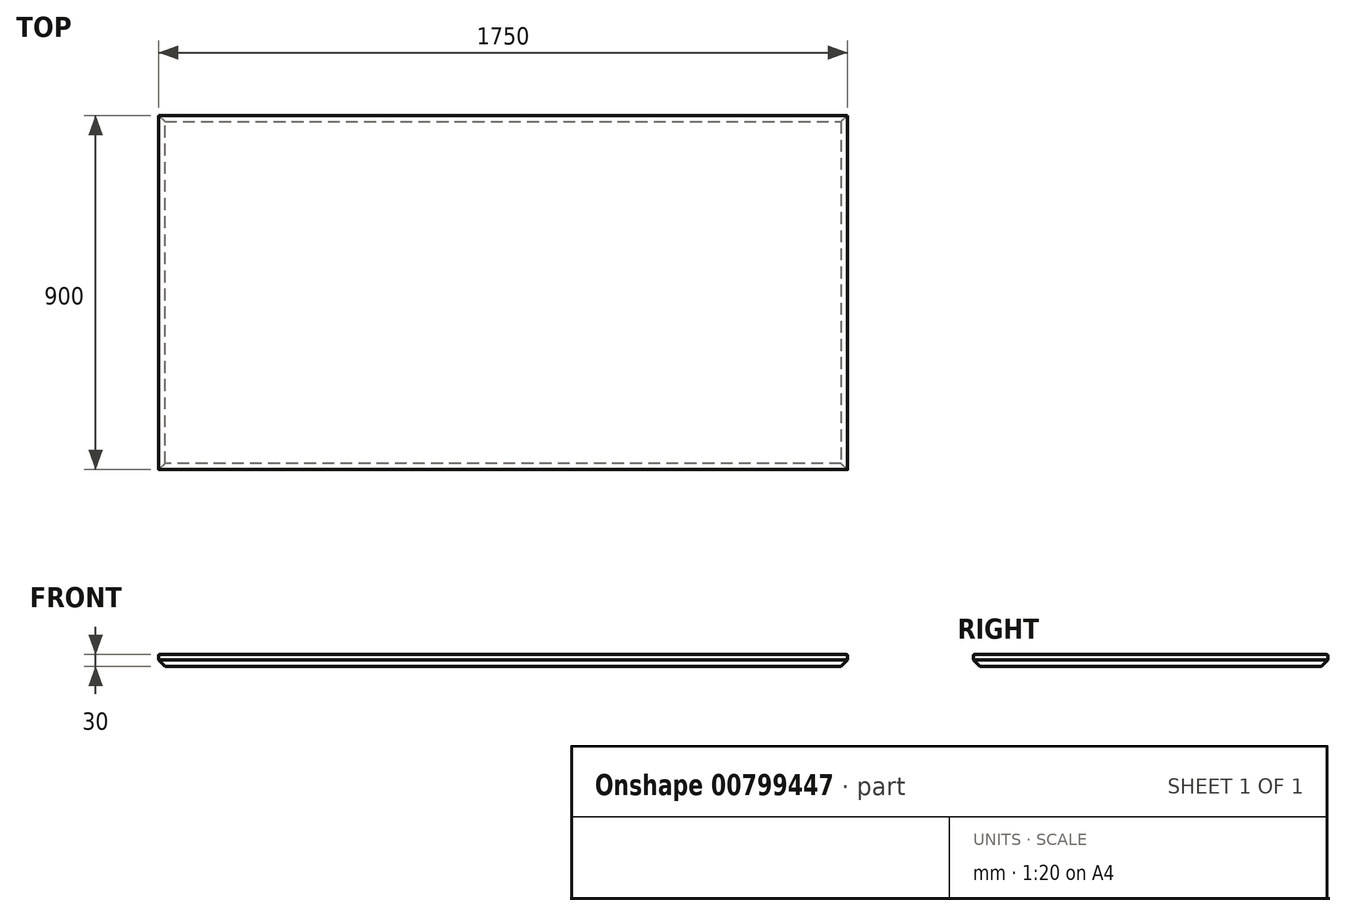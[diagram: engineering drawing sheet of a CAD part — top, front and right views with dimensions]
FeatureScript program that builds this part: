
annotation { "Feature Type Name" : "Feature", "Feature Type Description" : "" }
export const myFeature = defineFeature(function(context is Context, id is Id, definition is map)
    precondition{}
    {
        {
            var Q0;
            Q0=qCreatedBy(makeId("Top.planeOp"),FACE);
            var sketch = newSketch(context, id + "F0", { "sketchPlane" : qUnion([Q0])});
            skLineSegment(sketch, "E0.bottom", {"start": v(875, -450) * mm, "end": v(-875, -450) * mm});
            skLineSegment(sketch, "E0.top", {"start": v(875, 450) * mm, "end": v(-875, 450) * mm});
            skLineSegment(sketch, "E0.left", {"start": v(875, -450) * mm, "end": v(875, 450) * mm});
            skLineSegment(sketch, "E0.right", {"start": v(-875, -450) * mm, "end": v(-875, 450) * mm});
            skPoint(sketch, "E0.middle", {"position": v(0, 0) * mm});
            skSolve(sketch);
        }
        {
            var Q0;
            Q0=makeQuery(id+"F0.imprint","IMPRINT",FACE,{"disambiguationData":[TD([[makeQuery(id+"F0.imprint","IMPRINT",EDGE,{"derivedFrom":sQuery(id+"F0.wireOp",EDGE,"E0.bottom")}),-1.0]])]});
            extrude(context, id + "F1", {"entities" : qUnion([Q0]), "oppositeDirection" : true, "depth" : 30 * mm});
        }
        {
            var Q0;
            Q0=makeQuery(id+"F1.opExtrude","CAP_EDGE",EDGE,{"disambiguationData":[OSD([sQuery(id+"F0.wireOp",EDGE,"E0.bottom")])],"isStart":false});
            var Q1;
            Q1=makeQuery(id+"F1.opExtrude","CAP_EDGE",EDGE,{"disambiguationData":[OSD([sQuery(id+"F0.wireOp",EDGE,"E0.right")])],"isStart":false});
            var Q2;
            Q2=makeQuery(id+"F1.opExtrude","CAP_EDGE",EDGE,{"disambiguationData":[OSD([sQuery(id+"F0.wireOp",EDGE,"E0.top")])],"isStart":false});
            var Q3;
            Q3=makeQuery(id+"F1.opExtrude","CAP_EDGE",EDGE,{"disambiguationData":[OSD([sQuery(id+"F0.wireOp",EDGE,"E0.left")])],"isStart":false});
            chamfer(context, id + "F2", {"entities" : qUnion([Q0, Q1, Q2, Q3]), "width" : 16 * mm, "tangentPropagation" : true});
        }
        {
            var Q0;
            Q0=makeQuery(id+"F1.opExtrude","CAP_EDGE",EDGE,{"disambiguationData":[OSD([sQuery(id+"F0.wireOp",EDGE,"E0.top")])],"isStart":true});
            var Q1;
            Q1=makeQuery(id+"F1.opExtrude","CAP_EDGE",EDGE,{"disambiguationData":[OSD([sQuery(id+"F0.wireOp",EDGE,"E0.left")])],"isStart":true});
            var Q2;
            Q2=makeQuery(id+"F1.opExtrude","CAP_EDGE",EDGE,{"disambiguationData":[OSD([sQuery(id+"F0.wireOp",EDGE,"E0.bottom")])],"isStart":true});
            var Q3;
            Q3=makeQuery(id+"F1.opExtrude","CAP_EDGE",EDGE,{"disambiguationData":[OSD([sQuery(id+"F0.wireOp",EDGE,"E0.right")])],"isStart":true});
            fillet(context, id + "F3", {"entities" : qUnion([Q0, Q1, Q2, Q3]), "radius" : 2 * mm, "tangentPropagation" : true, "allowEdgeOverflow" : false});
        }
    });
